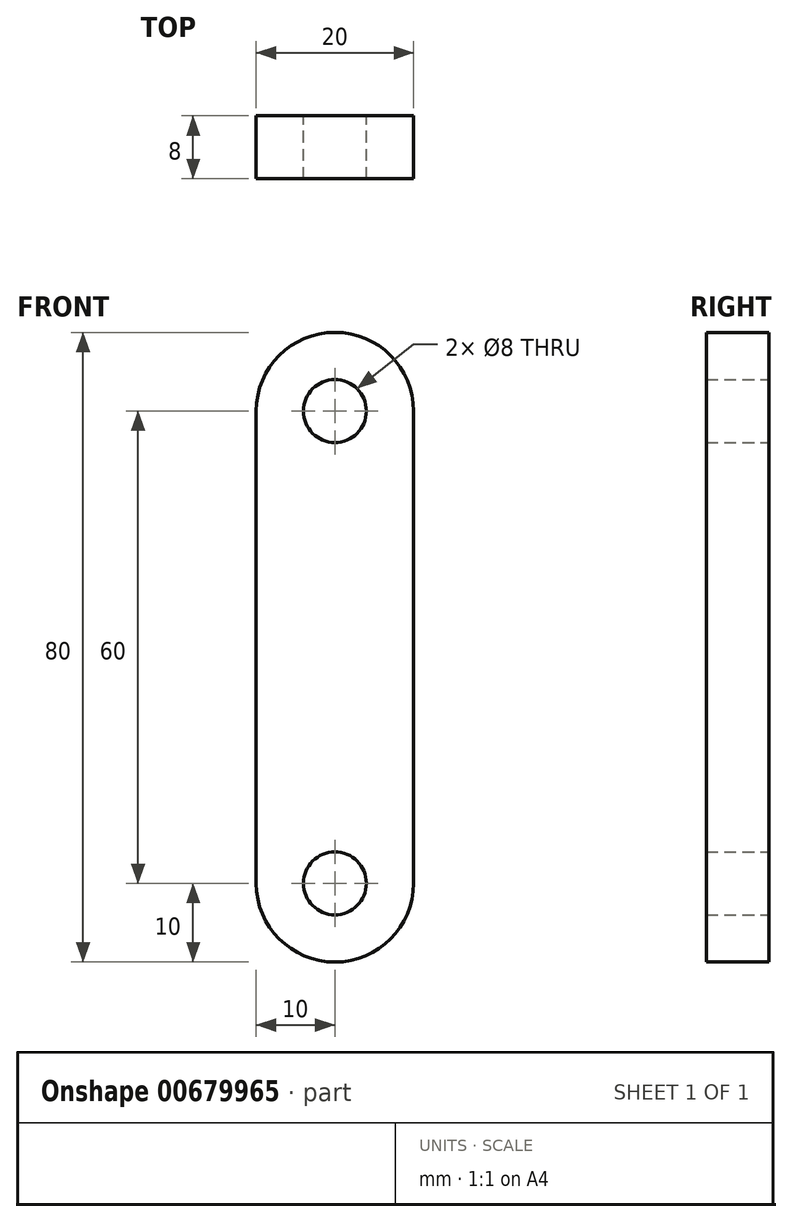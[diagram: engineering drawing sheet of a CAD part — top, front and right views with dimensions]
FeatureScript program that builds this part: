
annotation { "Feature Type Name" : "Feature", "Feature Type Description" : "" }
export const myFeature = defineFeature(function(context is Context, id is Id, definition is map)
    precondition{}
    {
        {
            var Q0;
            Q0=qCreatedBy(makeId("Front.planeOp"),FACE);
            var sketch = newSketch(context, id + "F0", { "sketchPlane" : qUnion([Q0])});
            skArc(sketch, "E0", {"start": v(-10, 0) * mm, "mid": v(0, -10) * mm, "end": v(10, 0) * mm});
            skCircle(sketch, "E1", {"center": v(0, 0) * mm, "radius": 4 * mm});
            skArc(sketch, "E2", {"start": v(10, 60) * mm, "mid": v(0, 70) * mm, "end": v(-10, 60) * mm});
            skCircle(sketch, "E3", {"center": v(0, 60) * mm, "radius": 4 * mm});
            skLineSegment(sketch, "E4", {"start": v(-10, 60) * mm, "end": v(-10, 0) * mm});
            skLineSegment(sketch, "E5", {"start": v(10, 0) * mm, "end": v(10, 60) * mm});
            skSolve(sketch);
        }
        {
            var Q0;
            Q0 = qSketchRegion(id + "F0", true);
            extrude(context, id + "F1", {"entities" : qUnion([Q0]), "depth" : 8 * mm, "offsetDistance" : 25.4 * mm});
        }
    });
